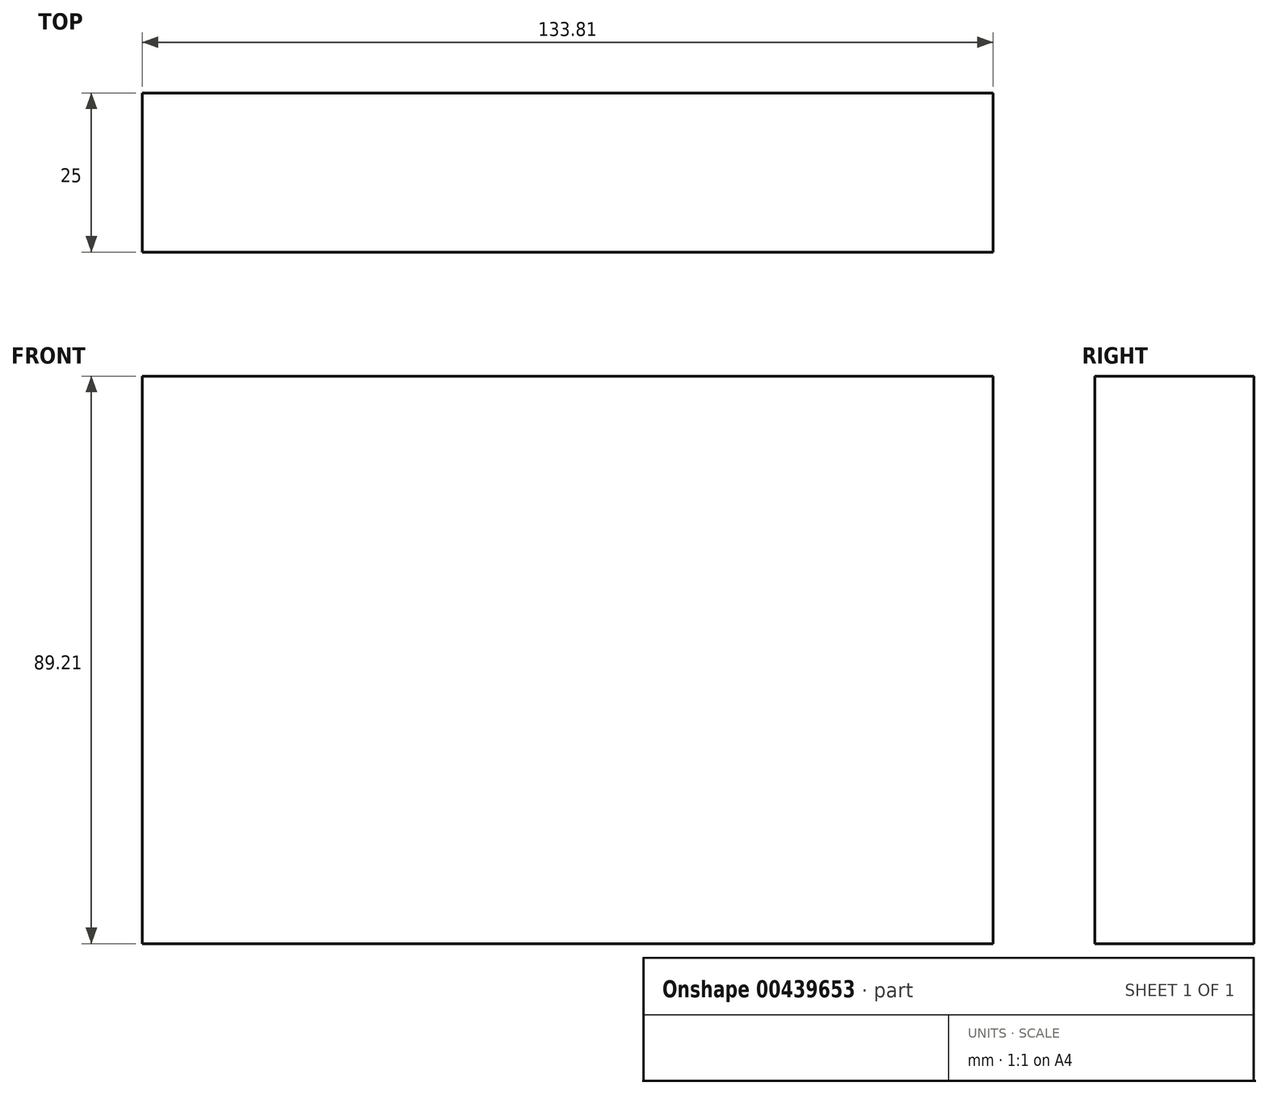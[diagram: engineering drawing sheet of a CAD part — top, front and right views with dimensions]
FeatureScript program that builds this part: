
annotation { "Feature Type Name" : "Feature", "Feature Type Description" : "" }
export const myFeature = defineFeature(function(context is Context, id is Id, definition is map)
    precondition{}
    {
        {
            var Q0;
            Q0=qCreatedBy(makeId("Front.planeOp"),FACE);
            var sketch = newSketch(context, id + "F0", { "sketchPlane" : qUnion([Q0])});
            skLineSegment(sketch, "E0.bottom", {"start": v(-64.52, -68.2) * mm, "end": v(69.3, -68.2) * mm});
            skLineSegment(sketch, "E0.top", {"start": v(-64.52, 21.02) * mm, "end": v(69.3, 21.02) * mm});
            skLineSegment(sketch, "E0.left", {"start": v(-64.52, -68.2) * mm, "end": v(-64.52, 21.02) * mm});
            skLineSegment(sketch, "E0.right", {"start": v(69.3, -68.2) * mm, "end": v(69.3, 21.02) * mm});
            skSolve(sketch);
        }
        {
            var Q0;
            Q0=makeQuery(id+"F0.imprint","IMPRINT",FACE,{"disambiguationData":[TD([[makeQuery(id+"F0.imprint","IMPRINT",EDGE,{"derivedFrom":sQuery(id+"F0.wireOp",EDGE,"E0.bottom")}),1.0]])]});
            extrude(context, id + "F1", {"entities" : qUnion([Q0]), "depth" : 25 * mm});
        }
    });
